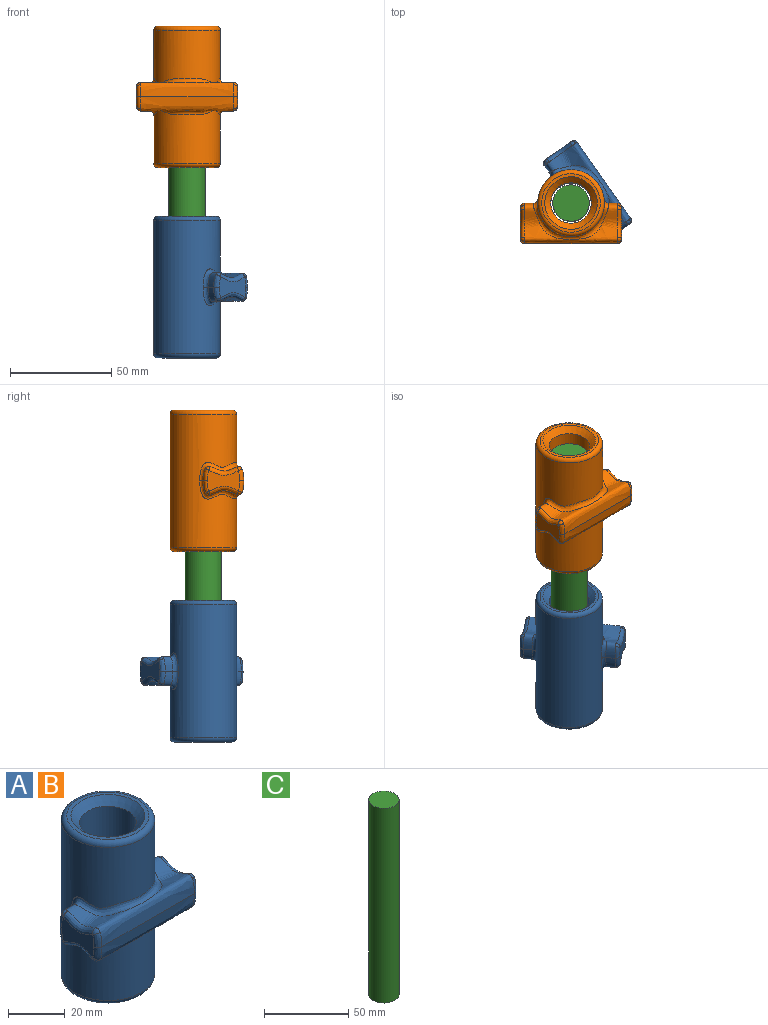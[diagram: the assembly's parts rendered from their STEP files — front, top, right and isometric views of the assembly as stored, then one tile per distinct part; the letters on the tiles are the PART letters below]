
ASSEMBLY  parts=3 mates=2
PART A: 34 faces, bbox 50x37.8x70 mm
  f0: cylinder r=16.47mm len=66mm, axis (0,0,-1), area 5945.4mm2, adj f27,f28,f29,f30
  f1: plane 28.93x28.93mm, normal (0,0,1), area 126.5mm2, adj f28,f32
  f2: plane 28.93x28.93mm, normal (0,0,-1), area 126.5mm2, adj f27,f33
  f3: extruded ~46x20mm, area 700.1mm2, adj f6,f10,f12,f14,f15,f16,f17,f18
  f4: plane 16x10.12mm, normal (1,0,0), area 115.6mm2, adj f18,f19,f20,f23,f24,f25
  f5: plane 16x10.12mm, normal (-1,0,0), area 115.6mm2, adj f8,f9,f10,f13,f14,f15
  f6: extruded ~46x20mm, area 700.1mm2, adj f3,f7,f8,f9,f11,f13,f20,f22
  f7: bspline ~2.02x2mm, area 2.8mm2, adj f6,f8,f9
  f8: bspline ~6.8x2.84mm, area 18.6mm2, adj f5,f6,f7,f10
  f9: bspline ~14.82x4.37mm, area 46.7mm2, adj f5,f6,f7,f11
  f10: bspline ~6.83x2.91mm, area 18.6mm2, adj f3,f5,f8,f12
  f11: bspline ~2.2x2.06mm, area 3.4mm2, adj f6,f9,f13
  f12: bspline ~2.02x2mm, area 2.8mm2, adj f3,f10,f14
  f13: bspline ~6.68x2.74mm, area 17.5mm2, adj f5,f6,f11,f15
  f14: bspline ~14.77x4.36mm, area 46.7mm2, adj f3,f5,f12,f16
  f15: bspline ~7.55x2.68mm, area 17.5mm2, adj f3,f5,f13,f16
  f16: bspline ~2.2x2.05mm, area 3.3mm2, adj f3,f14,f15
  f17: bspline ~2.02x2mm, area 2.8mm2, adj f3,f18,f19
  f18: bspline ~8.34x2.84mm, area 18.6mm2, adj f3,f4,f17,f20
  f19: bspline ~14.82x4.37mm, area 46.7mm2, adj f3,f4,f17,f21
  f20: bspline ~6.8x2.89mm, area 18.6mm2, adj f4,f6,f18,f22
  f21: bspline ~2.2x2.06mm, area 3.4mm2, adj f3,f19,f23
  f22: bspline ~2.02x2mm, area 2.8mm2, adj f6,f20,f24
  f23: bspline ~6.66x2.71mm, area 17.5mm2, adj f3,f4,f21,f25
  f24: bspline ~14.77x4.36mm, area 46.7mm2, adj f4,f6,f22,f26
  f25: bspline ~7.55x2.68mm, area 17.5mm2, adj f4,f6,f23,f26
  f26: bspline ~2.2x2.05mm, area 3.3mm2, adj f6,f24,f25
  f27: torus R=14.47mm, axis (0,0,1), area 310.7mm2, adj f0,f2
  f28: torus R=14.47mm, axis (0,0,1), area 310.7mm2, adj f0,f1
  f29: bspline ~36.93x19.77mm, area 216.7mm2, adj f0,f3,f30
  f30: bspline ~36.93x19.77mm, area 216.7mm2, adj f0,f6,f29
  f31: cylinder r=10mm len=64mm, axis (0,0,-1), area 4021.2mm2, adj f32,f33
  f32: cone r=10mm half-angle=45deg, axis (0,0,1), area 306.6mm2, adj f1,f31
  f33: cone r=10mm half-angle=45deg, axis (0,0,-1), area 306.6mm2, adj f2,f31
PART B: same geometry as A
PART C: 3 faces, bbox 18x18x141.3 mm
  f0: cylinder r=9mm len=141.3mm, axis (0,0,-1), area 7990.3mm2, adj f1,f2
  f1: plane 18x18mm, normal (0,0,1), area 254.5mm2, adj f0
  f2: plane 18x18mm, normal (0,0,-1), area 254.5mm2, adj f0
PLACE A rot(axis=(0.89,-0.46,0),180deg) t=(-18.08,42.83,91.67)mm
PLACE B t=(-18.08,42.83,185.9)mm
PLACE C rot(axis=(0,0,-1),180deg) t=(-18.08,42.83,132.55)mm
MATE cylindrical C.f0 <-> B.f0  axis (0,0,-1) through (-18.08,42.83,141.9)mm
MATE cylindrical C.f0 <-> A.f0  axis (0,0,-1) through (-18.08,42.83,141.9)mm
